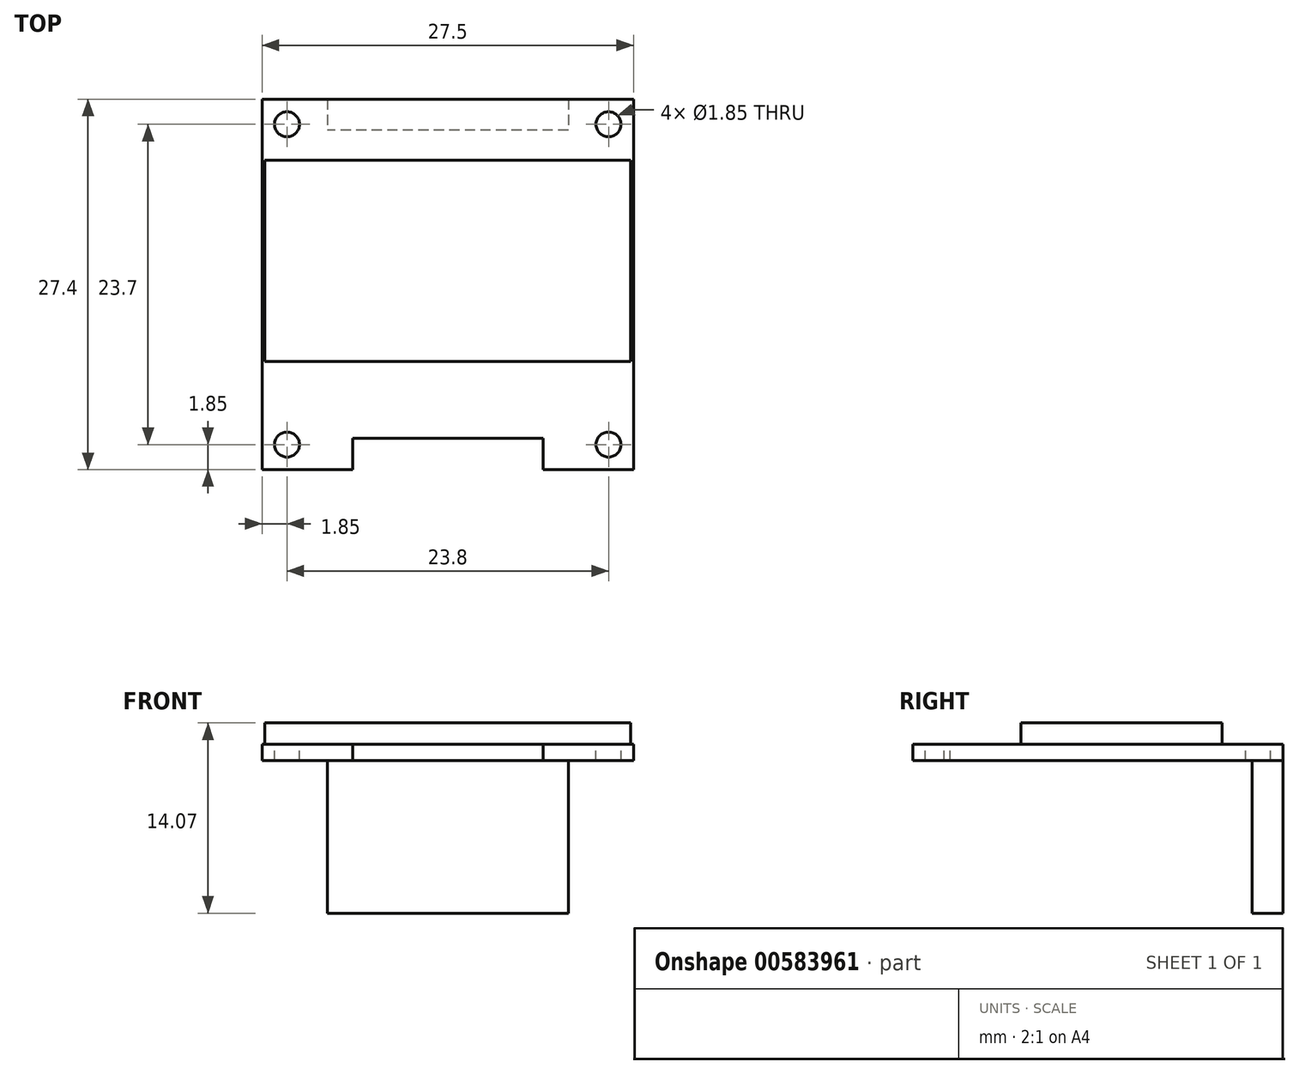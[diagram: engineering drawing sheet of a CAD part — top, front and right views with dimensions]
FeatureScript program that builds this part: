
annotation { "Feature Type Name" : "Feature", "Feature Type Description" : "" }
export const myFeature = defineFeature(function(context is Context, id is Id, definition is map)
    precondition{}
    {
        {
            var Q0;
            Q0=qCreatedBy(makeId("Top.planeOp"),FACE);
            var sketch = newSketch(context, id + "F0", { "sketchPlane" : qUnion([Q0])});
            skLineSegment(sketch, "E0.bottom", {"start": v(-13.75, 13.7) * mm, "end": v(13.75, 13.7) * mm});
            skLineSegment(sketch, "E0.top", {"start": v(-13.75, -13.7) * mm, "end": v(13.75, -13.7) * mm});
            skLineSegment(sketch, "E0.left", {"start": v(-13.75, 13.7) * mm, "end": v(-13.75, -13.7) * mm});
            skLineSegment(sketch, "E0.right", {"start": v(13.75, 13.7) * mm, "end": v(13.75, -13.7) * mm});
            skPoint(sketch, "E0.middle", {"position": v(0, 0) * mm});
            skSolve(sketch);
        }
        {
            var Q0;
            Q0 = qSketchRegion(id + "F0", true);
            extrude(context, id + "F1", {"entities" : qUnion([Q0]), "depth" : 1.22 * mm, "offsetDistance" : 25.4 * mm});
        }
        {
            var Q0;
            Q0=makeQuery(id+"F1.opExtrude","CAP_FACE",FACE,{"disambiguationData":[OSD([sQuery(id+"F0.wireOp",EDGE,"E0.bottom"),sQuery(id+"F0.wireOp",EDGE,"E0.top"),sQuery(id+"F0.wireOp",EDGE,"E0.left"),sQuery(id+"F0.wireOp",EDGE,"E0.right")])],"isStart":false});
            var sketch = newSketch(context, id + "F2", { "sketchPlane" : qUnion([Q0])});
            skLineSegment(sketch, "E1.bottom", {"start": v(-7.05, -13.7) * mm, "end": v(7.05, -13.7) * mm});
            skLineSegment(sketch, "E1.top", {"start": v(-7.05, -11.4) * mm, "end": v(7.05, -11.4) * mm});
            skLineSegment(sketch, "E1.left", {"start": v(-7.05, -13.7) * mm, "end": v(-7.05, -11.4) * mm});
            skLineSegment(sketch, "E1.right", {"start": v(7.05, -13.7) * mm, "end": v(7.05, -11.4) * mm});
            skSolve(sketch);
        }
        {
            var Q0;
            Q0 = qSketchRegion(id + "F2", true);
            extrude(context, id + "F3", {"entities" : qUnion([Q0]), "operationType" : NewBodyOperationType.REMOVE, "oppositeDirection" : true, "depth" : 25.4 * mm, "offsetDistance" : 25.4 * mm});
        }
        {
            var Q0;
            Q0=makeQuery(id+"F1.opExtrude","CAP_FACE",FACE,{"disambiguationData":[OSD([sQuery(id+"F0.wireOp",EDGE,"E0.bottom"),sQuery(id+"F0.wireOp",EDGE,"E0.top"),sQuery(id+"F0.wireOp",EDGE,"E0.left"),sQuery(id+"F0.wireOp",EDGE,"E0.right")])],"isStart":false});
            var sketch = newSketch(context, id + "F4", { "sketchPlane" : qUnion([Q0])});
            skLineSegment(sketch, "E2.bottom", {"start": v(-13.55, 9.18) * mm, "end": v(13.55, 9.18) * mm});
            skLineSegment(sketch, "E2.top", {"start": v(-13.55, -5.7) * mm, "end": v(13.55, -5.7) * mm});
            skLineSegment(sketch, "E2.left", {"start": v(-13.55, 9.18) * mm, "end": v(-13.55, -5.7) * mm});
            skLineSegment(sketch, "E2.right", {"start": v(13.55, 9.18) * mm, "end": v(13.55, -5.7) * mm});
            skSolve(sketch);
        }
        {
            var Q0;
            Q0 = qSketchRegion(id + "F4", true);
            extrude(context, id + "F5", {"entities" : qUnion([Q0]), "operationType" : NewBodyOperationType.ADD, "depth" : 1.57 * mm, "offsetDistance" : 25.4 * mm});
        }
        {
            var Q0;
            Q0=makeQuery(id+"F1.opExtrude","CAP_FACE",FACE,{"disambiguationData":[OSD([sQuery(id+"F0.wireOp",EDGE,"E0.bottom"),sQuery(id+"F0.wireOp",EDGE,"E0.top"),sQuery(id+"F0.wireOp",EDGE,"E0.left"),sQuery(id+"F0.wireOp",EDGE,"E0.right")])],"isStart":false});
            var sketch = newSketch(context, id + "F6", { "sketchPlane" : qUnion([Q0])});
            skPoint(sketch, "E3", {"position": v(-11.9, -11.85) * mm});
            skCircle(sketch, "E4", {"center": v(-11.9, -11.85) * mm, "radius": 1.85 * mm, "construction": true});
            skLineSegment(sketch, "E5.0", {"start": v(-13.75, -13.7) * mm, "end": v(-7.05, -13.7) * mm, "construction": true});
            skLineSegment(sketch, "E6.0", {"start": v(-13.75, 13.7) * mm, "end": v(-13.75, -13.7) * mm, "construction": true});
            skCircle(sketch, "E7", {"center": v(11.9, -11.85) * mm, "radius": 1.85 * mm, "construction": true});
            skLineSegment(sketch, "E8.0", {"start": v(13.75, 13.7) * mm, "end": v(13.75, -13.7) * mm, "construction": true});
            skLineSegment(sketch, "E9.0", {"start": v(-13.75, -13.7) * mm, "end": v(13.75, -13.7) * mm, "construction": true});
            skCircle(sketch, "E10", {"center": v(11.9, 11.85) * mm, "radius": 1.85 * mm, "construction": true});
            skCircle(sketch, "E11", {"center": v(-11.9, 11.85) * mm, "radius": 1.85 * mm, "construction": true});
            skLineSegment(sketch, "E12.0", {"start": v(-13.75, 13.7) * mm, "end": v(13.75, 13.7) * mm, "construction": true});
            skSolve(sketch);
        }
        {
            var Q0;
            Q0=sQuery(id+"F6.wireOp",VERTEX,"E3");
            var Q1;
            Q1=sQuery(id+"F6.wireOp",VERTEX,"E11.center");
            var Q2;
            Q2=sQuery(id+"F6.wireOp",VERTEX,"E10.center");
            var Q3;
            Q3=sQuery(id+"F6.wireOp",VERTEX,"E7.center");
            var Q4;
            Q4=makeQuery(id+"F1.opExtrude","SWEPT_BODY",BODY,{"disambiguationData":[OSD([sQuery(id+"F0.wireOp",EDGE,"E0.bottom"),sQuery(id+"F0.wireOp",EDGE,"E0.top"),sQuery(id+"F0.wireOp",EDGE,"E0.left"),sQuery(id+"F0.wireOp",EDGE,"E0.right")])]});
            hole(context, id + "F7", {"style" : HoleStyle.SIMPLE, "endStyle" : HoleEndStyle.THROUGH, "holeDiameter" : 1.85 * mm, "majorDiameter" : 6.35 * mm, "isTappedThrough" : true, "tappedDepth" : 12.7 * mm, "tapClearance" : 3, "locations" : qUnion([Q0, Q1, Q2, Q3]), "scope" : qUnion([Q4])});
        }
        {
            var Q0;
            Q0=makeQuery(id+"F1.opExtrude","CAP_FACE",FACE,{"disambiguationData":[OSD([sQuery(id+"F0.wireOp",EDGE,"E0.bottom"),sQuery(id+"F0.wireOp",EDGE,"E0.top"),sQuery(id+"F0.wireOp",EDGE,"E0.left"),sQuery(id+"F0.wireOp",EDGE,"E0.right")])],"isStart":true});
            var sketch = newSketch(context, id + "F8", { "sketchPlane" : qUnion([Q0])});
            skLineSegment(sketch, "E13.bottom", {"start": v(8.92, -13.7) * mm, "end": v(-8.92, -13.7) * mm});
            skLineSegment(sketch, "E13.top", {"start": v(8.92, -11.4) * mm, "end": v(-8.92, -11.4) * mm});
            skLineSegment(sketch, "E13.left", {"start": v(8.92, -13.7) * mm, "end": v(8.92, -11.4) * mm});
            skLineSegment(sketch, "E13.right", {"start": v(-8.92, -13.7) * mm, "end": v(-8.92, -11.4) * mm});
            skPoint(sketch, "E13.middle", {"position": v(0, -12.55) * mm});
            skSolve(sketch);
        }
        {
            var Q0;
            Q0 = qSketchRegion(id + "F8", true);
            extrude(context, id + "F9", {"entities" : qUnion([Q0]), "operationType" : NewBodyOperationType.ADD, "depth" : 11.28 * mm, "offsetDistance" : 25.4 * mm});
        }
    });
